# Revit family: QF_WASHTECH_GL WASHTECH 2014_cat
name_source: partatom
category: Specialty Equipment
revit_build: Autodesk Revit Architecture 2012 (Build: 20110916_2132(x64)
units: mm (PartAtom-declared; Revit-internal decimal feet)

## types (1)
- QF_WASHTECH_GL WASHTECH 2014_cat
    Apparent Power = 3600 VA
    Base Height = 25 mm
    Conn Conduit = Yes
    Cycle = 50 Hz
    Description = DISHWASHER
    FL Amps = 15 A
    Hot Water Connection Height = 0 mm  [stored 0 ft]
    Hot Water Size = 1"
    Indirect Waste Connection Height = 0 mm  [stored 0 ft]
    Indirect Waste Size = 2"
    Manufacturer = WASHTECH
    Max Overcurrent Protection = 0 A
    Min Ckt Ampacity = 0 A
    Model = GL WASHTECH 2014
    Phase = 1
    Volts = 240 V
    Watts = 3600 W
    Weight in Pounds = 0

note: [stored X ft] marks values corroborated as IEEE doubles in the binary element streams (Revit-internal decimal feet)

## geometry (parser evidence)
native form markers: Blend x2, Sweep x4
no freeform markers — native parametric forms only
